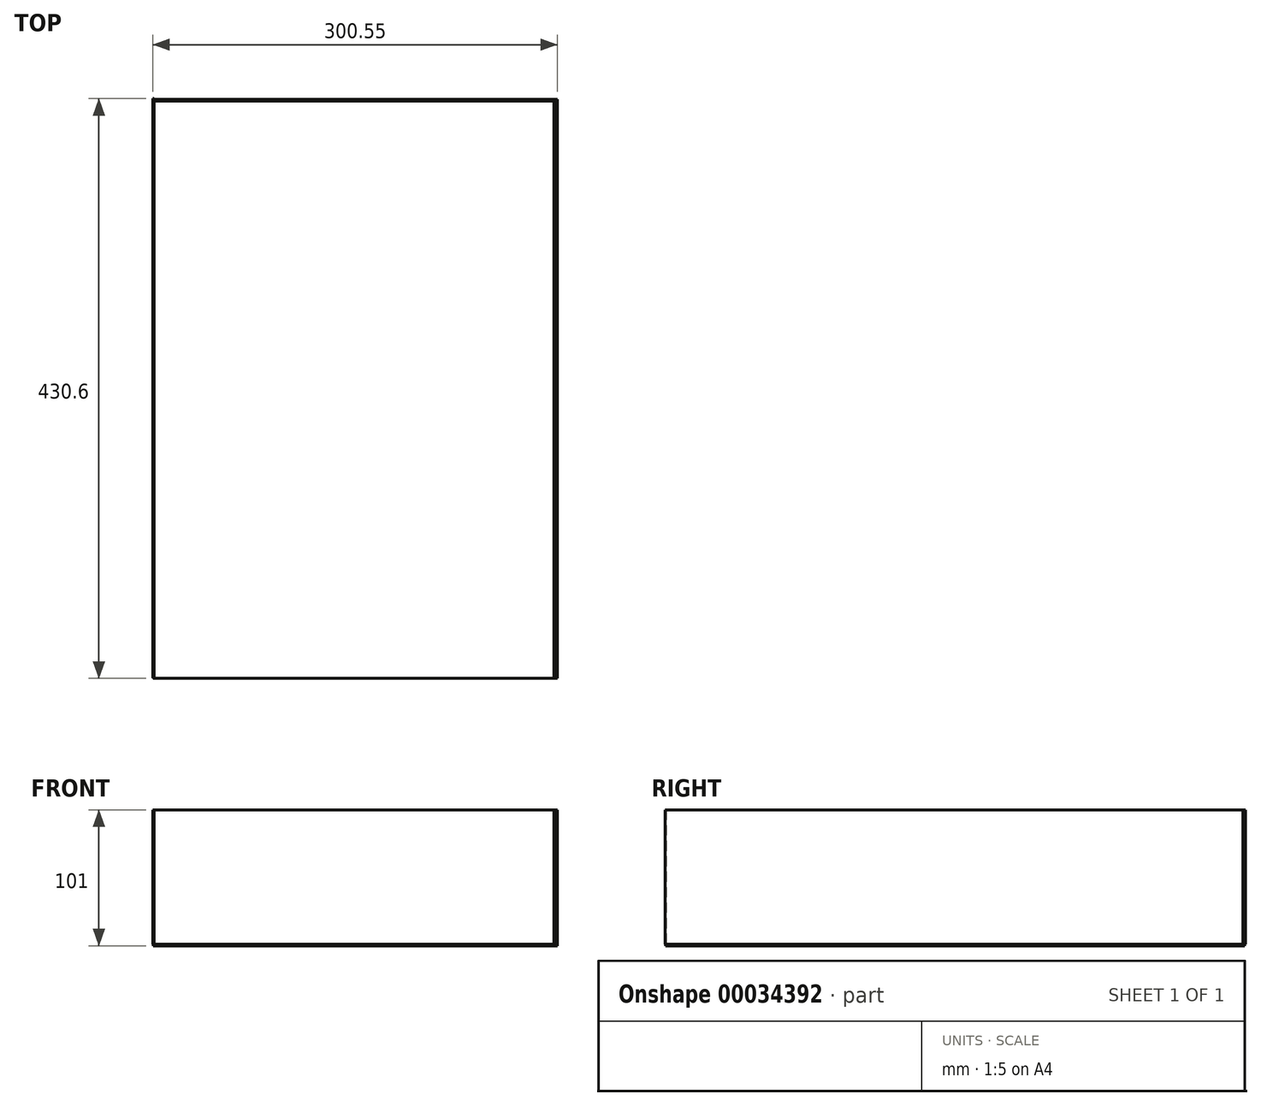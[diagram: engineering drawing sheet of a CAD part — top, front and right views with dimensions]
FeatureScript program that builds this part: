
annotation { "Feature Type Name" : "Feature", "Feature Type Description" : "" }
export const myFeature = defineFeature(function(context is Context, id is Id, definition is map)
    precondition{}
    {
        {
            var Q0;
            Q0=qCreatedBy(makeId("Top.planeOp"),FACE);
            var sketch = newSketch(context, id + "F0", { "sketchPlane" : qUnion([Q0])});
            skLineSegment(sketch, "E0.rect.bottom", {"start": v(-150, -215) * mm, "end": v(150, -215) * mm});
            skLineSegment(sketch, "E0.rect.top", {"start": v(-150, 215) * mm, "end": v(150, 215) * mm});
            skLineSegment(sketch, "E0.rect.left", {"start": v(-150, -215) * mm, "end": v(-150, 215) * mm});
            skLineSegment(sketch, "E0.rect.right", {"start": v(150, -215) * mm, "end": v(150, 215) * mm});
            skPoint(sketch, "E0.rect.middle", {"position": v(0, 0) * mm});
            skSolve(sketch);
        }
        {
            var Q0;
            Q0 = qSketchRegion(id + "F0", true);
            extrude(context, id + "F1", {"entities" : qUnion([Q0]), "oppositeDirection" : true, "depth" : 1 * mm});
        }
        {
            var Q0;
            Q0=qCreatedBy(makeId("Top.planeOp"),FACE);
            var sketch = newSketch(context, id + "F2", { "sketchPlane" : qUnion([Q0])});
            skLineSegment(sketch, "E1.bottom", {"start": v(-149.96, 214.76) * mm, "end": v(150.04, 214.76) * mm});
            skLineSegment(sketch, "E1.top", {"start": v(-149.96, 213.76) * mm, "end": v(150.04, 213.76) * mm});
            skLineSegment(sketch, "E1.left", {"start": v(-149.96, 214.76) * mm, "end": v(-149.96, 213.76) * mm});
            skLineSegment(sketch, "E1.right", {"start": v(150.04, 214.76) * mm, "end": v(150.04, 213.76) * mm});
            skSolve(sketch);
        }
        {
            var Q0;
            Q0 = qSketchRegion(id + "F2", true);
            extrude(context, id + "F3", {"entities" : qUnion([Q0]), "operationType" : NewBodyOperationType.ADD, "depth" : 100 * mm});
        }
        {
            var Q0;
            Q0=qCreatedBy(makeId("Top.planeOp"),FACE);
            var sketch = newSketch(context, id + "F4", { "sketchPlane" : qUnion([Q0])});
            skLineSegment(sketch, "E2.bottom", {"start": v(148.29, 214.9) * mm, "end": v(147.29, 214.9) * mm});
            skLineSegment(sketch, "E2.top", {"start": v(148.29, -215.1) * mm, "end": v(147.29, -215.1) * mm});
            skLineSegment(sketch, "E2.left", {"start": v(148.29, 214.9) * mm, "end": v(148.29, -215.1) * mm});
            skLineSegment(sketch, "E2.right", {"start": v(147.29, 214.9) * mm, "end": v(147.29, -215.1) * mm});
            skSolve(sketch);
        }
        {
            var Q0;
            Q0 = qSketchRegion(id + "F4", true);
            extrude(context, id + "F5", {"entities" : qUnion([Q0]), "operationType" : NewBodyOperationType.ADD, "depth" : 100 * mm});
        }
        {
            var Q0;
            Q0=qCreatedBy(makeId("Top.planeOp"),FACE);
            var sketch = newSketch(context, id + "F6", { "sketchPlane" : qUnion([Q0])});
            skLineSegment(sketch, "E3.bottom", {"start": v(-150.51, 215.5) * mm, "end": v(-149.51, 215.5) * mm});
            skLineSegment(sketch, "E3.top", {"start": v(-150.51, -214.5) * mm, "end": v(-149.51, -214.5) * mm});
            skLineSegment(sketch, "E3.left", {"start": v(-150.51, 215.5) * mm, "end": v(-150.51, -214.5) * mm});
            skLineSegment(sketch, "E3.right", {"start": v(-149.51, 215.5) * mm, "end": v(-149.51, -214.5) * mm});
            skSolve(sketch);
        }
        {
            var Q0;
            Q0 = qSketchRegion(id + "F6", true);
            extrude(context, id + "F7", {"entities" : qUnion([Q0]), "operationType" : NewBodyOperationType.ADD, "depth" : 100 * mm});
        }
    });
